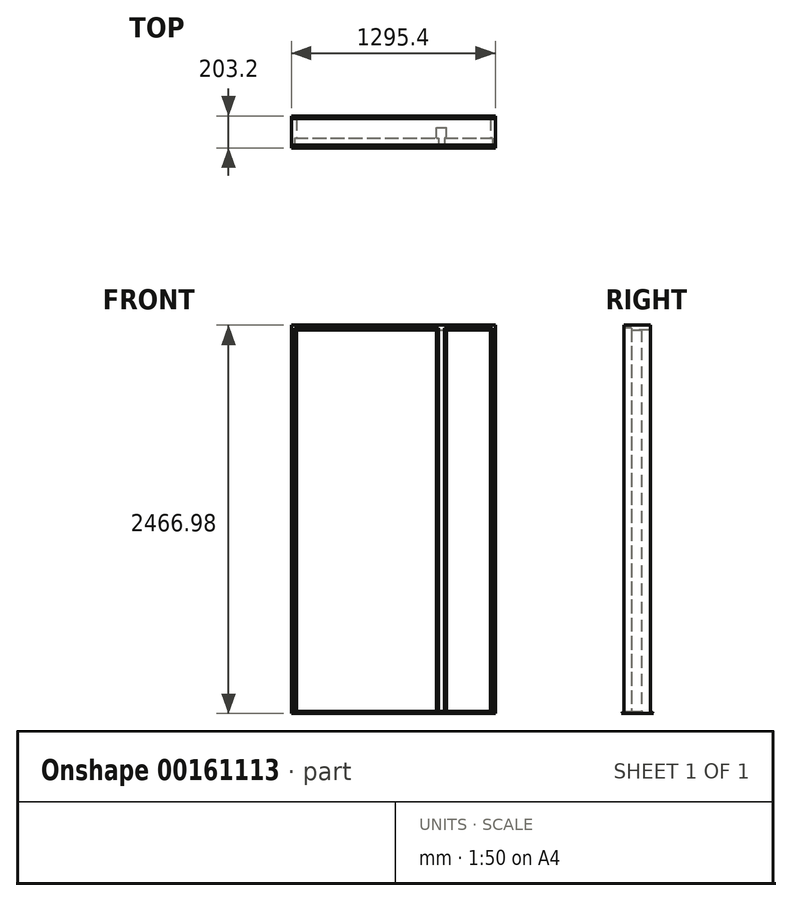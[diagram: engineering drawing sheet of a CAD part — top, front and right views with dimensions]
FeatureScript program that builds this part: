
annotation { "Feature Type Name" : "Feature", "Feature Type Description" : "" }
export const myFeature = defineFeature(function(context is Context, id is Id, definition is map)
    precondition{}
    {
        {
            var Q0;
            Q0=qCreatedBy(makeId("Top.planeOp"),FACE);
            var sketch = newSketch(context, id + "F0", { "sketchPlane" : qUnion([Q0])});
            skLineSegment(sketch, "E0", {"start": v(0, 0) * mm, "end": v(0, 168.28) * mm});
            skLineSegment(sketch, "E1", {"start": v(-31.75, 46.04) * mm, "end": v(-19.05, 46.04) * mm});
            skLineSegment(sketch, "E2", {"start": v(-19.05, 46.04) * mm, "end": v(-19.05, 0) * mm});
            skLineSegment(sketch, "E3", {"start": v(-19.05, 0) * mm, "end": v(0, 0) * mm});
            skLineSegment(sketch, "E4", {"start": v(-476.25, 0) * mm, "end": v(-476.25, 102.45) * mm, "construction": true});
            skLineSegment(sketch, "E5", {"start": v(0, 168.28) * mm, "end": v(-31.75, 168.28) * mm});
            skLineSegment(sketch, "E6", {"start": v(-31.75, 168.28) * mm, "end": v(-31.75, 46.04) * mm});
            skLineSegment(sketch, "E7.MirrorCS", {"start": v(-933.45, 46.04) * mm, "end": v(-933.45, 0) * mm});
            skLineSegment(sketch, "E8.MirrorCS", {"start": v(-920.75, 46.04) * mm, "end": v(-933.45, 46.04) * mm});
            skLineSegment(sketch, "E9.MirrorCS", {"start": v(-920.75, 168.28) * mm, "end": v(-920.75, 46.04) * mm});
            skLineSegment(sketch, "E10.MirrorCS", {"start": v(-952.5, 168.28) * mm, "end": v(-920.75, 168.28) * mm});
            skLineSegment(sketch, "E11.MirrorCS", {"start": v(-952.5, 0) * mm, "end": v(-952.5, 168.28) * mm});
            skLineSegment(sketch, "E12.MirrorCS", {"start": v(-933.45, 0) * mm, "end": v(-952.5, 0) * mm});
            skSolve(sketch);
        }
        {
            var Q0;
            Q0=qCreatedBy(makeId("Top.planeOp"),FACE);
            var sketch = newSketch(context, id + "F1", { "sketchPlane" : qUnion([Q0])});
            skLineSegment(sketch, "E13.0.0", {"start": v(-952.5, 0) * mm, "end": v(-933.45, 0) * mm});
            skLineSegment(sketch, "E13.0.1", {"start": v(-933.45, 0) * mm, "end": v(-933.45, 46.04) * mm});
            skLineSegment(sketch, "E13.0.2", {"start": v(-933.45, 46.04) * mm, "end": v(-920.75, 46.04) * mm});
            skLineSegment(sketch, "E13.0.3", {"start": v(-920.75, 46.04) * mm, "end": v(-920.75, 168.28) * mm});
            skLineSegment(sketch, "E13.0.4", {"start": v(-920.75, 168.28) * mm, "end": v(-952.5, 168.28) * mm});
            skLineSegment(sketch, "E13.0.5", {"start": v(-952.5, 168.28) * mm, "end": v(-952.5, 0) * mm});
            skLineSegment(sketch, "E14.0", {"start": v(-19.05, 46.04) * mm, "end": v(-19.05, 0) * mm});
            skLineSegment(sketch, "E15.0", {"start": v(-31.75, 46.04) * mm, "end": v(-19.05, 46.04) * mm});
            skLineSegment(sketch, "E16", {"start": v(-31.75, 46.04) * mm, "end": v(-31.75, 111.13) * mm});
            skLineSegment(sketch, "E17.0", {"start": v(0, 0) * mm, "end": v(0, 168.28) * mm, "construction": true});
            skLineSegment(sketch, "E18.MirrorCS", {"start": v(31.75, 46.04) * mm, "end": v(31.75, 111.13) * mm});
            skLineSegment(sketch, "E19.MirrorCS", {"start": v(31.75, 46.04) * mm, "end": v(19.05, 46.04) * mm});
            skLineSegment(sketch, "E20.MirrorCS", {"start": v(19.05, 46.04) * mm, "end": v(19.05, 0) * mm});
            skLineSegment(sketch, "E21", {"start": v(-31.75, 111.13) * mm, "end": v(31.75, 111.13) * mm});
            skLineSegment(sketch, "E22", {"start": v(19.05, 0) * mm, "end": v(-19.05, 0) * mm});
            skPoint(sketch, "E23", {"position": v(323.85, 0) * mm});
            skLineSegment(sketch, "E24", {"start": v(-933.45, 0) * mm, "end": v(323.85, 0) * mm, "construction": true});
            skLineSegment(sketch, "E25", {"start": v(-304.8, 0) * mm, "end": v(-304.8, 103.65) * mm, "construction": true});
            skLineSegment(sketch, "E26.MirrorCS", {"start": v(323.85, 46.04) * mm, "end": v(311.15, 46.04) * mm});
            skLineSegment(sketch, "E27.MirrorCS", {"start": v(342.9, 0) * mm, "end": v(323.85, 0) * mm});
            skLineSegment(sketch, "E28.MirrorCS", {"start": v(342.9, 168.28) * mm, "end": v(342.9, 0) * mm});
            skLineSegment(sketch, "E29.MirrorCS", {"start": v(311.15, 168.28) * mm, "end": v(342.9, 168.28) * mm});
            skLineSegment(sketch, "E30.MirrorCS", {"start": v(311.15, 46.04) * mm, "end": v(311.15, 168.28) * mm});
            skLineSegment(sketch, "E31.MirrorCS", {"start": v(323.85, 0) * mm, "end": v(323.85, 46.04) * mm});
            skSolve(sketch);
        }
        {
            var Q0;
            Q0 = qSketchRegion(id + "F1", true);
            extrude(context, id + "F2", {"entities" : qUnion([Q0]), "depth" : 2454.27 * mm});
        }
        {
            var Q0;
            Q0=qCreatedBy(makeId("Front.planeOp"),FACE);
            var sketch = newSketch(context, id + "F3", { "sketchPlane" : qUnion([Q0])});
            skPoint(sketch, "E32.0", {"position": v(-952.5, 2454.28) * mm});
            skPoint(sketch, "E33.0", {"position": v(-31.75, 2454.28) * mm});
            skLineSegment(sketch, "E34", {"start": v(-952.5, 2454.28) * mm, "end": v(-492.13, 1993.9) * mm});
            skLineSegment(sketch, "E35", {"start": v(-492.12, 1993.9) * mm, "end": v(-31.75, 2454.28) * mm});
            skLineSegment(sketch, "E36", {"start": v(-952.5, 2454.28) * mm, "end": v(-31.75, 2454.28) * mm});
            skPoint(sketch, "E37.0", {"position": v(31.75, 2454.28) * mm});
            skPoint(sketch, "E38.0", {"position": v(342.9, 2454.28) * mm});
            skLineSegment(sketch, "E39", {"start": v(31.75, 2454.28) * mm, "end": v(187.32, 2298.7) * mm});
            skLineSegment(sketch, "E40", {"start": v(187.33, 2298.7) * mm, "end": v(342.9, 2454.28) * mm});
            skLineSegment(sketch, "E41", {"start": v(31.75, 2454.28) * mm, "end": v(342.9, 2454.28) * mm});
            skSolve(sketch);
        }
        {
            var Q0;
            Q0=qSketchRegion(id+"F3",true);
            extrude(context, id + "F4", {"entities" : qUnion([Q0]), "operationType" : NewBodyOperationType.REMOVE, "endBound" : BoundingType.THROUGH_ALL, "oppositeDirection" : true, "depth" : 25.4 * mm});
        }
        {
            var Q0;
            Q0=qCreatedBy(makeId("Right.planeOp"),FACE);
            var sketch = newSketch(context, id + "F5", { "sketchPlane" : qUnion([Q0])});
            skLineSegment(sketch, "E42.0.0", {"start": v(168.28, 2454.28) * mm, "end": v(168.28, 2422.53) * mm});
            skLineSegment(sketch, "E42.0.1", {"start": v(168.28, 2422.53) * mm, "end": v(46.04, 2422.53) * mm});
            skLineSegment(sketch, "E42.0.2", {"start": v(46.04, 2422.53) * mm, "end": v(46.04, 2435.23) * mm});
            skLineSegment(sketch, "E42.0.3", {"start": v(46.04, 2435.23) * mm, "end": v(0, 2435.23) * mm});
            skLineSegment(sketch, "E42.0.4", {"start": v(0, 2435.23) * mm, "end": v(0, 2454.28) * mm});
            skLineSegment(sketch, "E42.0.5", {"start": v(0, 2454.28) * mm, "end": v(168.28, 2454.28) * mm});
            skSolve(sketch);
        }
        {
            var Q0;
            Q0=qSketchRegion(id+"F5",true);
            var Q1;
            Q1=makeQuery(id+"F2.opExtrude","SWEPT_FACE",FACE,{"disambiguationData":[OSD([sQuery(id+"F1.wireOp",EDGE,"E13.0.5")])]});
            var Q2;
            Q2=makeQuery(id+"F2.opExtrude","SWEPT_FACE",FACE,{"disambiguationData":[OSD([sQuery(id+"F1.wireOp",EDGE,"E28.MirrorCS")])]});
            extrude(context, id + "F6", {"entities" : qUnion([Q0]), "operationType" : NewBodyOperationType.ADD, "endBound" : BoundingType.UP_TO_SURFACE, "oppositeDirection" : true, "endBoundEntityFace" : qUnion([Q1]), "depth" : 914.4 * mm, "hasSecondDirection" : true, "secondDirectionBound" : SecondDirectionBoundingType.UP_TO_SURFACE, "secondDirectionOppositeDirection" : false, "secondDirectionBoundEntityFace" : qUnion([Q2]), "secondDirectionDepth" : 25.4 * mm});
        }
        {
            var Q0;
            Q0=qCreatedBy(makeId("Right.planeOp"),FACE);
            var sketch = newSketch(context, id + "F7", { "sketchPlane" : qUnion([Q0])});
            skPoint(sketch, "E43.0", {"position": v(84.14, 0) * mm});
            skLineSegment(sketch, "E44", {"start": v(84.14, 0) * mm, "end": v(84.14, -12.7) * mm, "construction": true});
            skLineSegment(sketch, "E45", {"start": v(84.14, -12.7) * mm, "end": v(185.74, -12.7) * mm});
            skLineSegment(sketch, "E46", {"start": v(185.74, -12.7) * mm, "end": v(169.86, 0) * mm});
            skLineSegment(sketch, "E47", {"start": v(169.86, 0) * mm, "end": v(84.14, 0) * mm});
            skLineSegment(sketch, "E48.MirrorCS", {"start": v(-1.59, 0) * mm, "end": v(84.14, 0) * mm});
            skLineSegment(sketch, "E49.MirrorCS", {"start": v(84.14, -12.7) * mm, "end": v(-17.46, -12.7) * mm});
            skLineSegment(sketch, "E50.MirrorCS", {"start": v(-17.46, -12.7) * mm, "end": v(-1.59, 0) * mm});
            skSolve(sketch);
        }
        {
            var Q0;
            Q0=qSketchRegion(id+"F7",true);
            var Q1;
            Q1=makeQuery(id+"F2.opExtrude","SWEPT_FACE",FACE,{"disambiguationData":[OSD([sQuery(id+"F1.wireOp",EDGE,"E28.MirrorCS")])]});
            var Q2;
            Q2=makeQuery(id+"F2.opExtrude","SWEPT_FACE",FACE,{"disambiguationData":[OSD([sQuery(id+"F1.wireOp",EDGE,"E13.0.5")])]});
            extrude(context, id + "F8", {"entities" : qUnion([Q0]), "operationType" : NewBodyOperationType.ADD, "endBound" : BoundingType.UP_TO_SURFACE, "endBoundEntityFace" : qUnion([Q1]), "depth" : 25.4 * mm, "hasSecondDirection" : true, "secondDirectionBound" : SecondDirectionBoundingType.UP_TO_SURFACE, "secondDirectionOppositeDirection" : true, "secondDirectionBoundEntityFace" : qUnion([Q2]), "secondDirectionDepth" : 25.4 * mm});
        }
    });
